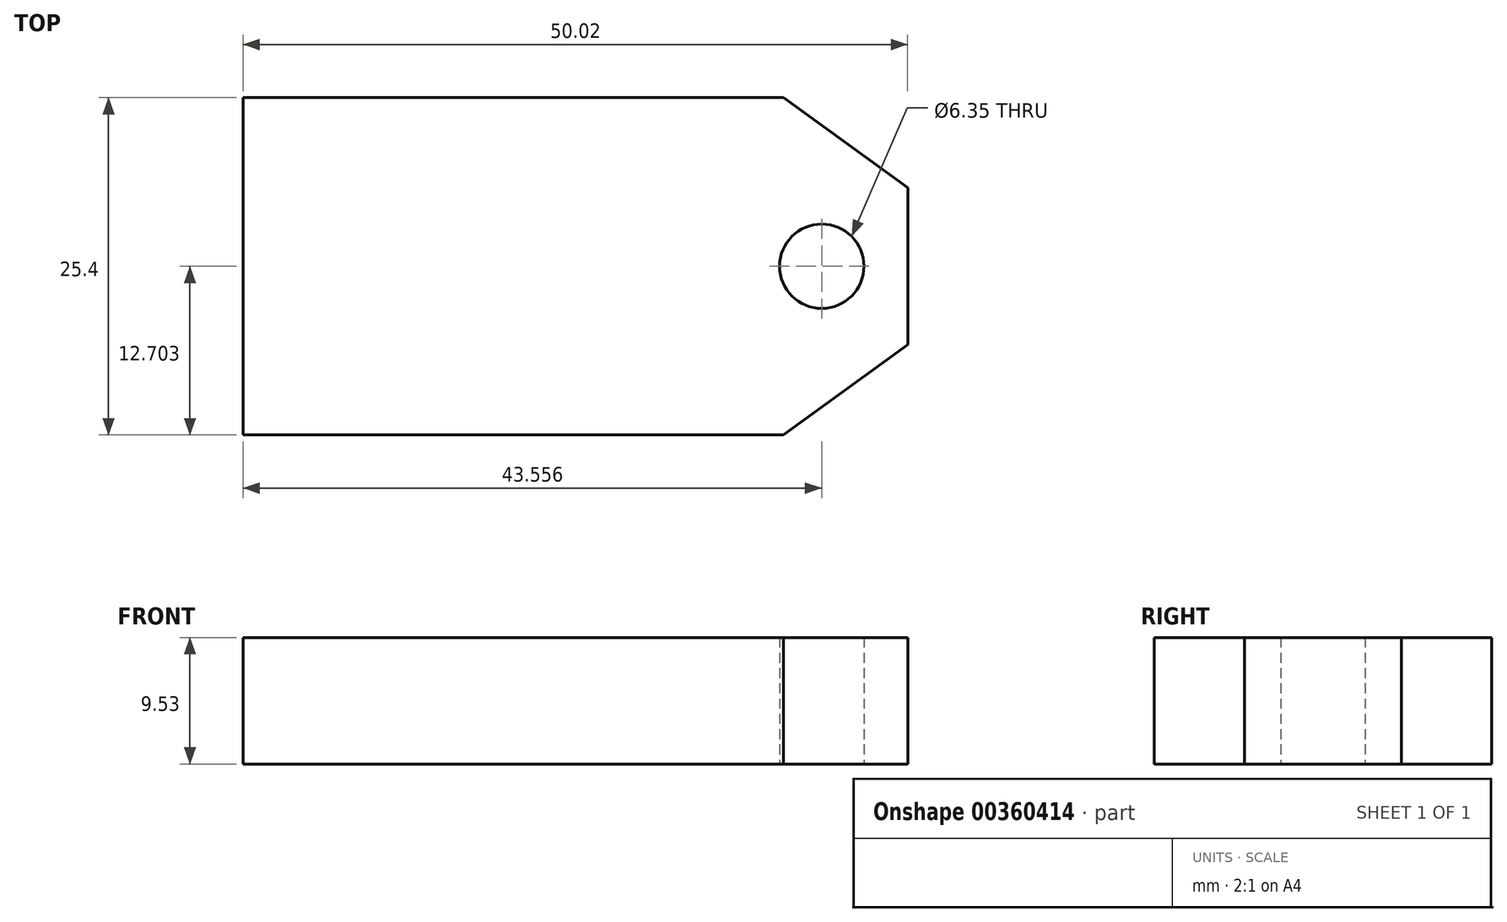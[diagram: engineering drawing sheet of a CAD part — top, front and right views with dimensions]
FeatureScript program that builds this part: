
annotation { "Feature Type Name" : "Feature", "Feature Type Description" : "" }
export const myFeature = defineFeature(function(context is Context, id is Id, definition is map)
    precondition{}
    {
        {
            var Q0;
            Q0=qCreatedBy(makeId("Top.planeOp"),FACE);
            var sketch = newSketch(context, id + "F0", { "sketchPlane" : qUnion([Q0])});
            skLineSegment(sketch, "E0", {"start": v(-15.27, -25.73) * mm, "end": v(-15.27, -38.43) * mm});
            skLineSegment(sketch, "E1", {"start": v(-15.27, -38.43) * mm, "end": v(25.4, -38.43) * mm});
            skLineSegment(sketch, "E2", {"start": v(25.4, -38.43) * mm, "end": v(34.75, -31.63) * mm});
            skLineSegment(sketch, "E3", {"start": v(34.75, -31.63) * mm, "end": v(34.75, -25.73) * mm});
            skLineSegment(sketch, "E4", {"start": v(-22.5, -25.73) * mm, "end": v(40.66, -25.73) * mm, "construction": true});
            skLineSegment(sketch, "E5.MirrorCS", {"start": v(-15.27, -25.73) * mm, "end": v(-15.27, -13.03) * mm});
            skLineSegment(sketch, "E6.MirrorCS", {"start": v(-15.27, -13.03) * mm, "end": v(25.4, -13.03) * mm});
            skLineSegment(sketch, "E7.MirrorCS", {"start": v(25.4, -13.03) * mm, "end": v(34.75, -19.82) * mm});
            skLineSegment(sketch, "E8.MirrorCS", {"start": v(34.75, -19.82) * mm, "end": v(34.75, -25.73) * mm});
            skCircle(sketch, "E9", {"center": v(28.29, -25.73) * mm, "radius": 3.18 * mm});
            skSolve(sketch);
        }
        {
            var Q0;
            Q0=makeQuery(id+"F0.imprint","IMPRINT",FACE,{"disambiguationData":[TD([[makeQuery(id+"F0.imprint","IMPRINT",EDGE,{"derivedFrom":sQuery(id+"F0.wireOp",EDGE,"E0")}),1.0]])]});
            extrude(context, id + "F1", {"entities" : qUnion([Q0]), "depth" : 9.52 * mm});
        }
        {
            var Q0;
            Q0=makeQuery(id+"F1.opExtrude","CAP_FACE",FACE,{"disambiguationData":[OSD([sQuery(id+"F0.wireOp",EDGE,"E0"),sQuery(id+"F0.wireOp",EDGE,"E1"),sQuery(id+"F0.wireOp",EDGE,"E2"),sQuery(id+"F0.wireOp",EDGE,"E3"),sQuery(id+"F0.wireOp",EDGE,"E5.MirrorCS"),sQuery(id+"F0.wireOp",EDGE,"E6.MirrorCS"),sQuery(id+"F0.wireOp",EDGE,"E7.MirrorCS"),sQuery(id+"F0.wireOp",EDGE,"E8.MirrorCS"),sQuery(id+"F0.wireOp",EDGE,"E9")])],"isStart":false});
            var sketch = newSketch(context, id + "F2", { "sketchPlane" : qUnion([Q0])});
            skText(sketch, "E10", { "text": "Punahou", "fontName": "OpenSans-Regular.ttf"});
            const initialGuessF2  = {"E10": [-0.0566, -0.03741, 1, 0, 0.00654]};
            skSetInitialGuess(sketch, initialGuessF2);
            skSolve(sketch);
        }
        {
            var Q0;
            Q0=qSketchRegion(id+"F2",true);
            extrude(context, id + "F3", {"entities" : qUnion([Q0]), "operationType" : NewBodyOperationType.REMOVE, "oppositeDirection" : true, "depth" : 3.17 * mm});
        }
    });
